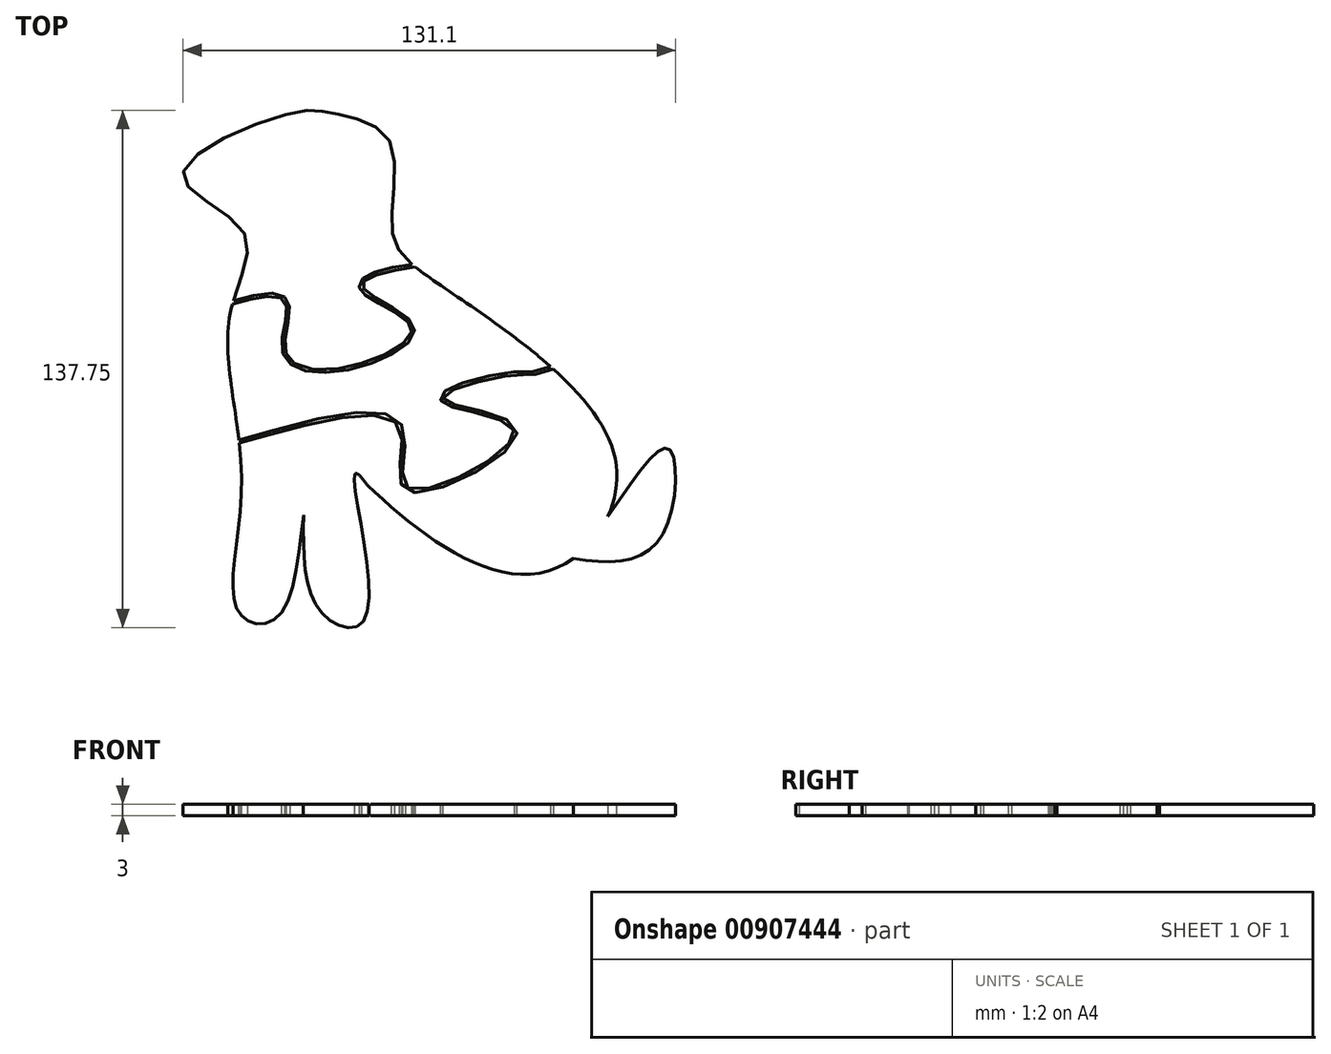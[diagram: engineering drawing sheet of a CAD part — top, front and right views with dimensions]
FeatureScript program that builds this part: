
annotation { "Feature Type Name" : "Feature", "Feature Type Description" : "" }
export const myFeature = defineFeature(function(context is Context, id is Id, definition is map)
    precondition{}
    {
        {
            var Q0;
            Q0=qCreatedBy(makeId("Top.planeOp"),FACE);
            var sketch = newSketch(context, id + "F0", { "sketchPlane" : qUnion([Q0])});
            skFitSpline(sketch, "E0", {"points": [v(-39.44, 36.59) * mm, v(-55.54, 51.5) * mm, v(-27.06, 68.04) * mm, v(-14.76, 67.87) * mm, v(-0.72, 60.86) * mm, v(0, 37.74) * mm, v(9.9, 24.41) * mm, v(59.15, -22.47) * mm, v(41.12, -53.93) * mm, v(0, -36.8) * mm, v(-19.81, -24.66) * mm, v(-29.32, -64.88) * mm, v(-40.43, -65.16) * mm, v(-39.92, -30.98) * mm, v(-43.1, 14.19) * mm, v(-39.44, 36.59) * mm]});
            skFitSpline(sketch, "E1", {"points": [v(-23.47, -38.88) * mm, v(-18.46, -65.08) * mm, v(-7.13, -66.5) * mm, v(-9.8, -28.03) * mm, v(-6.45, -30.98) * mm], "startDerivative": vector(-0.85, -99.27) * mm, "endDerivative": vector(31.32, -42.9) * mm});
            skFitSpline(sketch, "E2", {"points": [v(57.52, -39.24) * mm, v(73.58, -21.17) * mm, v(74.3, -38.52) * mm, v(65.15, -50.09) * mm, v(48.37, -50.41) * mm], "startDerivative": vector(70.46, 100.8) * mm, "endDerivative": vector(-77.19, 12.42) * mm});
            skLineSegment(sketch, "E3", {"start": v(28.84, 8.26) * mm, "end": v(31.48, 9.34) * mm});
            skLineSegment(sketch, "E4", {"start": v(-40.32, -16.74) * mm, "end": v(-41.17, -14.82) * mm});
            skFitSpline(sketch, "E5", {"points": [v(-42.38, 17.3) * mm, v(-28.44, 17.95) * mm, v(-28.88, 3.9) * mm, v(-10.55, 0) * mm, v(5.84, 11.54) * mm, v(-7.86, 21.98) * mm, v(6.24, 27.15) * mm], "startDerivative": vector(105.52, 28.24) * mm, "endDerivative": vector(114.55, 13.78) * mm});
            skFitSpline(sketch, "E6", {"points": [v(-40.55, -19.73) * mm, v(1.66, -14.82) * mm, v(3.94, -32.4) * mm, v(33.38, -16.38) * mm, v(13.78, -8.02) * mm, v(32.17, -1.62) * mm, v(42.95, 0) * mm], "startDerivative": vector(151.2, 38.2) * mm, "endDerivative": vector(141.7, 63.7) * mm});
            skFitSpline(sketch, "E7.0", {"points": [v(-42.59, 18.08) * mm, v(-41.5, 18.38) * mm, v(-39.16, 19) * mm, v(-36.2, 19.66) * mm, v(-33.96, 20) * mm, v(-32.37, 20.11) * mm, v(-30.9, 20.06) * mm, v(-29.81, 19.84) * mm, v(-29.02, 19.51) * mm, v(-28.48, 19.18) * mm, v(-28, 18.74) * mm, v(-27.63, 18.2) * mm, v(-27.38, 17.6) * mm, v(-27.19, 16.75) * mm, v(-27.14, 15.62) * mm, v(-27.27, 14.16) * mm, v(-27.52, 12.6) * mm, v(-27.83, 11) * mm, v(-28.12, 9.37) * mm, v(-28.35, 7.78) * mm, v(-28.44, 6.28) * mm, v(-28.36, 5.16) * mm, v(-28.2, 4.36) * mm, v(-27.95, 3.64) * mm, v(-27.49, 2.84) * mm, v(-26.69, 2.01) * mm, v(-25.64, 1.3) * mm, v(-23.93, 0.53) * mm, v(-21.26, -0.07) * mm, v(-17.42, -0.21) * mm, v(-13.88, 0.15) * mm, v(-10.94, 0.71) * mm, v(-7.97, 1.45) * mm, v(-4.3, 2.67) * mm, v(-0.98, 4.2) * mm, v(1.29, 5.53) * mm, v(2.74, 6.57) * mm, v(3.9, 7.63) * mm, v(4.74, 8.66) * mm, v(5.2, 9.64) * mm, v(5.3, 10.36) * mm, v(5.22, 10.91) * mm, v(5.07, 11.33) * mm, v(4.81, 11.79) * mm, v(4.32, 12.42) * mm, v(3.45, 13.26) * mm, v(2.08, 14.27) * mm, v(0.5, 15.27) * mm, v(-1.2, 16.25) * mm, v(-2.92, 17.2) * mm, v(-4.57, 18.13) * mm, v(-5.81, 18.89) * mm, v(-6.68, 19.49) * mm, v(-7.27, 19.94) * mm, v(-7.78, 20.4) * mm, v(-8.2, 20.88) * mm, v(-8.48, 21.32) * mm, v(-8.62, 21.72) * mm, v(-8.7, 22.15) * mm, v(-8.67, 22.7) * mm, v(-8.43, 23.27) * mm, v(-8.06, 23.76) * mm, v(-7.6, 24.17) * mm, v(-7.07, 24.55) * mm, v(-6.25, 25) * mm, v(-5.07, 25.53) * mm, v(-3.42, 26.08) * mm, v(-1.6, 26.58) * mm, v(0.34, 27.02) * mm, v(2.98, 27.52) * mm, v(4.94, 27.8) * mm, v(6.15, 27.95) * mm]});
            skFitSpline(sketch, "E8.0", {"points": [v(-40.75, -18.95) * mm, v(-39.19, -18.56) * mm, v(-35.5, -17.54) * mm, v(-28.85, -15.66) * mm, v(-21.64, -13.79) * mm, v(-15.64, -12.5) * mm, v(-11.1, -11.82) * mm, v(-7.9, -11.53) * mm, v(-4.96, -11.49) * mm, v(-2.34, -11.76) * mm, v(-0.46, -12.3) * mm, v(0.83, -12.97) * mm, v(1.67, -13.6) * mm, v(2.38, -14.38) * mm, v(2.9, -15.29) * mm, v(3.24, -16.27) * mm, v(3.53, -17.66) * mm, v(3.61, -19.5) * mm, v(3.46, -21.83) * mm, v(3.2, -24.17) * mm, v(2.95, -26.4) * mm, v(2.87, -28.43) * mm, v(3.04, -29.8) * mm, v(3.33, -30.65) * mm, v(3.63, -31.15) * mm, v(4, -31.52) * mm, v(4.5, -31.81) * mm, v(5.2, -32.02) * mm, v(6.39, -32.15) * mm, v(8.27, -32.03) * mm, v(10.97, -31.45) * mm, v(13.97, -30.49) * mm, v(17.13, -29.2) * mm, v(20.32, -27.68) * mm, v(23.4, -25.96) * mm, v(26.26, -24.12) * mm, v(28.75, -22.24) * mm, v(30.41, -20.69) * mm, v(31.43, -19.5) * mm, v(32.01, -18.67) * mm, v(32.4, -17.9) * mm, v(32.61, -17.22) * mm, v(32.64, -16.75) * mm, v(32.58, -16.42) * mm, v(32.47, -16.1) * mm, v(32.22, -15.69) * mm, v(31.73, -15.17) * mm, v(31.04, -14.67) * mm, v(29.9, -14.01) * mm, v(28.1, -13.27) * mm, v(25.58, -12.48) * mm, v(22.9, -11.8) * mm, v(20.66, -11.27) * mm, v(18.97, -10.87) * mm, v(17.77, -10.58) * mm, v(16.66, -10.28) * mm, v(15.66, -9.98) * mm, v(14.8, -9.66) * mm, v(14.17, -9.37) * mm, v(13.74, -9.1) * mm, v(13.45, -8.88) * mm, v(13.2, -8.6) * mm, v(12.99, -8.25) * mm, v(12.88, -7.83) * mm, v(12.92, -7.41) * mm, v(13.05, -7.05) * mm, v(13.24, -6.73) * mm, v(13.47, -6.46) * mm, v(13.82, -6.13) * mm, v(14.34, -5.74) * mm, v(15.1, -5.3) * mm, v(15.98, -4.88) * mm, v(16.97, -4.46) * mm, v(18.42, -3.9) * mm, v(20.44, -3.25) * mm, v(23.05, -2.52) * mm, v(25.73, -1.87) * mm, v(28.33, -1.34) * mm, v(30.33, -1.02) * mm, v(31.76, -0.85) * mm, v(32.74, -0.76) * mm, v(33.6, -0.72) * mm, v(34.65, -0.7) * mm, v(35.76, -0.74) * mm, v(36.9, -0.78) * mm, v(37.98, -0.73) * mm, v(39.17, -0.54) * mm, v(40.64, -0.1) * mm, v(41.9, 0.4) * mm, v(42.63, 0.73) * mm]});
            skSolve(sketch);
        }
        {
            var Q0;
            {var subQ0=sQuery(id+"F0.wireOp",EDGE,"E7.0");var subQ1=sQuery(id+"F0.wireOp",EDGE,"E0");var subQ2=makeQuery(id+"F0.imprint","INTERSECT",VERTEX,{"disambiguationData":[OD(0.0)],"derivedFrom":[subQ1,subQ0]});Q0=makeQuery(id+"F0.imprint","IMPRINT",FACE,{"disambiguationData":[TD([[makeQuery(id+"F0.imprint","IMPRINT",EDGE,{"disambiguationData":[TD([[subQ2,1.0]])],"derivedFrom":subQ1}),-1.0]])]});}
            var Q1;
            {var subQ2=sQuery(id+"F0.wireOp",EDGE,"E5");Q1=makeQuery(id+"F0.imprint","IMPRINT",FACE,{"disambiguationData":[TD([[makeQuery(id+"F0.imprint","IMPRINT",EDGE,{"derivedFrom":subQ2}),-1.0]])]});}
            var Q2;
            {var subQ4=sQuery(id+"F0.wireOp",EDGE,"E6");Q2=makeQuery(id+"F0.imprint","IMPRINT",FACE,{"disambiguationData":[TD([[makeQuery(id+"F0.imprint","IMPRINT",EDGE,{"derivedFrom":subQ4}),-1.0]])]});}
            var Q3;
            {var subQ0=sQuery(id+"F0.wireOp",EDGE,"E1");var subQ1=sQuery(id+"F0.wireOp",EDGE,"E0");var subQ2=makeQuery(id+"F0.imprint","INTERSECT",VERTEX,{"disambiguationData":[OD(0.0)],"derivedFrom":[subQ1,subQ0]});Q3=makeQuery(id+"F0.imprint","IMPRINT",FACE,{"disambiguationData":[TD([[makeQuery(id+"F0.imprint","IMPRINT",EDGE,{"disambiguationData":[TD([[subQ2,1.0]])],"derivedFrom":subQ1}),1.0]])]});}
            var Q4;
            {var subQ0=sQuery(id+"F0.wireOp",EDGE,"E2");Q4=makeQuery(id+"F0.imprint","IMPRINT",FACE,{"disambiguationData":[TD([[makeQuery(id+"F0.imprint","IMPRINT",EDGE,{"derivedFrom":subQ0}),-1.0]])]});}
            extrude(context, id + "F1", {"entities" : qUnion([Q0, Q1, Q2, Q3, Q4]), "depth" : 3 * mm, "offsetDistance" : 25 * mm});
        }
    });
